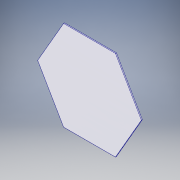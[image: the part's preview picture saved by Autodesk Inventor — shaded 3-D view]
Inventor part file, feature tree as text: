
AUTODESK INVENTOR PART (.ipt)
format: ipt  version: 2019 (Build 230136000, 136)  size: 96,256 bytes
history: native  units: mm
features: extrude x1, sketch x1
ambient origin geometry x8: Origin, YZ Plane, XZ Plane, XY Plane, X Axis, Y Axis, Z Axis, Center Point
bodies: Solid1 (feature_tree)
feature tree (2):
  extrude  "Extrusion1"  Depth=2.0mm TaperAngle=0.0deg
  sketch  "Sketch1"  dims[d0=192.0mm d1=2.0mm d2=0.0mm]
